# Revit family: Bathtub-Drop_In-DXV-Aqua_Moment-D12015328.415
name_source: partatom
category: Plumbing Fixtures
revit_build: Autodesk Revit 2014 (Build: 20130308_1515(x64)
units: mm (PartAtom-declared; Revit-internal decimal feet)

## types (1)
- D12015328.415
    Assembly Code = D2010510
    Body Finish = Acrylic-DXV-415-Canvas White
    Body Material = Acrylic-DXV-415-Canvas White
    CW Connection = Yes
    CWFU = 5
    Default Elevation = 0"
    Description = DXV Aqua Moment™ Drop-In Airbath with Waterfall
    Drain Finish = Metal-DXV-002-Polished Chrome
    Drain Material = Metal-DXV-002-Polished Chrome
    HW Connection = No
    HWFU = 0
    Height = 22 1/2"
    Installation Type = Floor Mounted
    Length = 35 1/2"
    Manufacturer = DXV
    Model = D12015328.415
    Price = Prices may vary. Please consult manufacturer representative for most up to date price list.
    Product Documentation Link = https://dxv01.blob.core.windows.net
    Product Page URL = https://www.dxv.com
    URL = www.dxv.com
    Vent Connection = No
    WFU = 5
    Waste Connection = Yes
    Waste Connection Diameter = 3"
    Waste Connection Radius = 1 1/2"
    Width = 71 1/2"

## geometry (parser evidence)
native form markers: Sweep x1
no freeform markers — native parametric forms only
